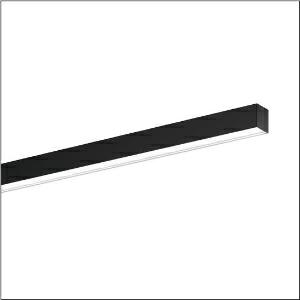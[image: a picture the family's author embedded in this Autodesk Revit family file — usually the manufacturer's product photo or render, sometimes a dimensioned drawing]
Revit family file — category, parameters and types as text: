
# Revit family: silica_r__21_51mx20tbt2b_b214
name_source: partatom
category: Lighting Fixtures
units: mm (PartAtom-declared; Revit-internal decimal feet)

## family parameters
Cut with Voids When Loaded = No
Host = Face
Light Source = No
Part Type = Normal
Room Calculation Point = No
Round Connector Dimension = Use Diameter
Shared = No

## types (1)
- --- (1 x LED, 3000 lm, 25.6 W, 6500K)
    Apparent Load = 26 VA
    CIE Flux Codes = 48 79 96 100 100
    Color Rendering = 80
    Color Temperature = 6500K
    Default Elevation = 1800 mm
    Description = Silica® 21, office luminaire, primary optical cover: cover, of PMMA, opal, light emission: direct distribution, primary light characteristic: symmetric, installation type: surface-mounted, LED, rated luminous flux: 3.000lm, luminous efficacy: 112lm/W, light colour: 8tw, colour temperature: 2700..6500K, control gear: ECG DALI, with terminal, 3+2-pole, max. 2.5mm², mains connection: 220..240V, AC, 50/60Hz, rated input power: 26.9W, luminaire housing, of aluminium, jet black (RAL 9005), length: 1.504mm, width: 53mm, height: 53mm, protection rating (complete): IP20, insulation class (complete): insulation class I (protective earthing), certification: CE, permissible operating ambient temperature: 0..+35°C, standard: EN 50419, packaging unit: 1 piece
    Height = 0 mm  [stored 0 ft]
    Lamp = 1 x LED
    Lamp Light Flux = 3000 lm
    Lamp Power = 25.6 W
    Lamp count = 1
    Length = 1504 mm
    Luminous efficacy = 117 lm/W
    Manufacturer = Siteco
    ModVariant = No
    Model = 51MX20TBT2B
    Mounting Place = Ceiling
    Mounting Type = Recessed
    Number of Poles = 1
    OnlyDefault = Yes
    Power Factor = 1
    Product Name = Silica® 21
    Product group = office luminaire | ceiling recessed
    ProductGroupID = 400
    Protection Class = Protection class I
    Protection Degree = IP 20
    RLX_Detail_Level = 1
    RLX_Emergency_Light_Flux = 0 lm
    RLX_Emergency_Type = 0
    RLX_Emergency_Type_DB = No
    RlxData = <blob elided: 25653 chars, md5=2ad21190>
    Socket = socket
    Standby Power = 0 W
    System Light Flux = 3000 lm
    System Power = 26 W
    Type Comments = individual setting
    Type Image = l_1335925.jpg
    URL = http://relux.com
    VarID = @adj_109489
    Voltage = 0 V
    Weight = 0.00 kg
    Width = 53 mm

note: [stored X ft] marks values corroborated as IEEE doubles in the binary element streams (Revit-internal decimal feet)

## geometry (parser evidence)
native form markers: Blend x4, Sweep x10
no freeform markers — native parametric forms only
